# Revit family: Univers-IP30-syst-Surface_mounted-NoHosted-CH-en
name_source: partatom
category: Electrical Equipment
units: mm (PartAtom-declared; Revit-internal decimal feet)

## family parameters
Always vertical = Yes
Cut with Voids When Loaded = No
Panel Configuration = Two Columns, Circuits Across
Part Type = Panelboard
Room Calculation Point = No
Round Connector Dimension = Use Diameter
Shared = No
Work Plane-Based = Yes

## types (20) — shared parameters
Default Elevation = 1219 mm
EF000003 - Mounting method = EV000384 - Surface mounted (plaster)
EF000007 - Colour = EV000202 - White
EF000049 - Depth = 161 mm  [stored 0.528215 ft]
EF000116 - RAL-number = 9010
EF000118 - With mounting plate = No
EF000339 - Type of cover = EV000494 - None
EF001062 - EMC-version = No
EF001088 - Extension possible = No
EF001131 - Internal depth = 161 mm  [stored 0.528215 ft]
EF001134 - DIN-rail = No
EF001596 - Material housing = EV000179 - Steel
EF002950 - Width in number of modular spacings = 12
EF004462 - Type of closure = EV000154 - Other
EF005474 - Degree of protection (IP) = EV006410 - IP30
EF006244 - Transparent cover/door = No
EF006306 - With lock = No
EF009212 - Cover model = EV009916 - With notch
EF015776 - Earthing terminal block = No
EF015777 - Neutral terminal block = No
EF015941 - Signal passing door = No
HG000002 - With door or cover = No
HG000003 - Range = Univers
HG000005 - Thickness = 3 mm  [stored 0.00984252 ft]
HG000006 - Flush mounted = No
HG000009 - Double swing door = No
HG000010 - Asymmetric doors = No
HG000011 - Empty rows from bottom = No
Manufacturer = Hager
Type Comments = Univers
zero-valued in all types: EF000218 - Built-in depth, EF000332 - Built-in height, EF000846 - Built-in width, HG000007 - Number of empty columns, HG000008 - Number of empty rows

## per-type parameters (varying)
| type | EF000008 - Width | EF000040 - Height | EF000266 - Number of rows | HG000001 - Number of columns | HG000004 - Manufacturer reference | Model |
| Surface mounted IP30 W1050 H1100 D161 12 Modular spacings - FWB74T1S | 1050 mm | 1100 mm | 28 | 4 | FWB74T1S | FWB74T1S |
| Surface mounted IP30 W1050 H500 D161 12 Modular spacings - FWB34T1S | 1050 mm | 500 mm  [stored 1.64042 ft] | 12 | 4 | FWB34T1S | FWB34T1S |
| Surface mounted IP30 W1050 H650 D161 12 Modular spacings - FWB44T1S | 1050 mm | 650 mm  [stored 2.13255 ft] | 16 | 4 | FWB44T1S | FWB44T1S |
| Surface mounted IP30 W1050 H800 D161 12 Modular spacings - FWB54T1S | 1050 mm | 800 mm  [stored 2.62467 ft] | 20 | 4 | FWB54T1S | FWB54T1S |
| Surface mounted IP30 W1050 H950 D161 12 Modular spacings - FWB64T1S | 1050 mm | 950 mm  [stored 3.1168 ft] | 24 | 4 | FWB64T1S | FWB64T1S |
| Surface mounted IP30 W300 H1100 D161 12 Modular spacings - FWB71T1S | 300 mm | 1100 mm | 7 | 1 | FWB71T1S | FWB71T1S |
| Surface mounted IP30 W300 H500 D161 12 Modular spacings - FWB31T1S | 300 mm | 500 mm  [stored 1.64042 ft] | 3 | 1 | FWB31T1S | FWB31T1S |
| Surface mounted IP30 W300 H650 D161 12 Modular spacings - FWB41T1S | 300 mm | 650 mm  [stored 2.13255 ft] | 4 | 1 | FWB41T1S | FWB41T1S |
| Surface mounted IP30 W300 H800 D161 12 Modular spacings - FWB51T1S | 300 mm | 800 mm  [stored 2.62467 ft] | 5 | 1 | FWB51T1S | FWB51T1S |
| Surface mounted IP30 W300 H950 D161 12 Modular spacings - FWB61T1S | 300 mm | 950 mm  [stored 3.1168 ft] | 6 | 1 | FWB61T1S | FWB61T1S |
| Surface mounted IP30 W550 H1100 D161 12 Modular spacings - FWB72T1S | 550 mm | 1100 mm | 14 | 2 | FWB72T1S | FWB72T1S |
| Surface mounted IP30 W550 H500 D161 12 Modular spacings - FWB32T1S | 550 mm | 500 mm  [stored 1.64042 ft] | 6 | 2 | FWB32T1S | FWB32T1S |
| Surface mounted IP30 W550 H650 D161 12 Modular spacings - FWB42T1S | 550 mm | 650 mm  [stored 2.13255 ft] | 8 | 2 | FWB42T1S | FWB42T1S |
| Surface mounted IP30 W550 H800 D161 12 Modular spacings - FWB52T1S | 550 mm | 800 mm  [stored 2.62467 ft] | 10 | 2 | FWB52T1S | FWB52T1S |
| Surface mounted IP30 W550 H950 D161 12 Modular spacings - FWB62T1S | 550 mm | 950 mm  [stored 3.1168 ft] | 12 | 2 | FWB62T1S | FWB62T1S |
| Surface mounted IP30 W800 H1100 D161 12 Modular spacings - FWB73T1S | 800 mm  [stored 2.62467 ft] | 1100 mm | 21 | 3 | FWB73T1S | FWB73T1S |
| Surface mounted IP30 W800 H500 D161 12 Modular spacings - FWB33T1S | 800 mm  [stored 2.62467 ft] | 500 mm  [stored 1.64042 ft] | 9 | 3 | FWB33T1S | FWB33T1S |
| Surface mounted IP30 W800 H650 D161 12 Modular spacings - FWB43T1S | 800 mm  [stored 2.62467 ft] | 650 mm  [stored 2.13255 ft] | 12 | 3 | FWB43T1S | FWB43T1S |
| Surface mounted IP30 W800 H800 D161 12 Modular spacings - FWB53T1S | 800 mm  [stored 2.62467 ft] | 800 mm  [stored 2.62467 ft] | 15 | 3 | FWB53T1S | FWB53T1S |
| Surface mounted IP30 W800 H950 D161 12 Modular spacings - FWB63T1S | 800 mm  [stored 2.62467 ft] | 950 mm  [stored 3.1168 ft] | 18 | 3 | FWB63T1S | FWB63T1S |

note: [stored X ft] marks values corroborated as IEEE doubles in the binary element streams (Revit-internal decimal feet)

## geometry (parser evidence)
native form markers: Sweep x16
no freeform markers — native parametric forms only
